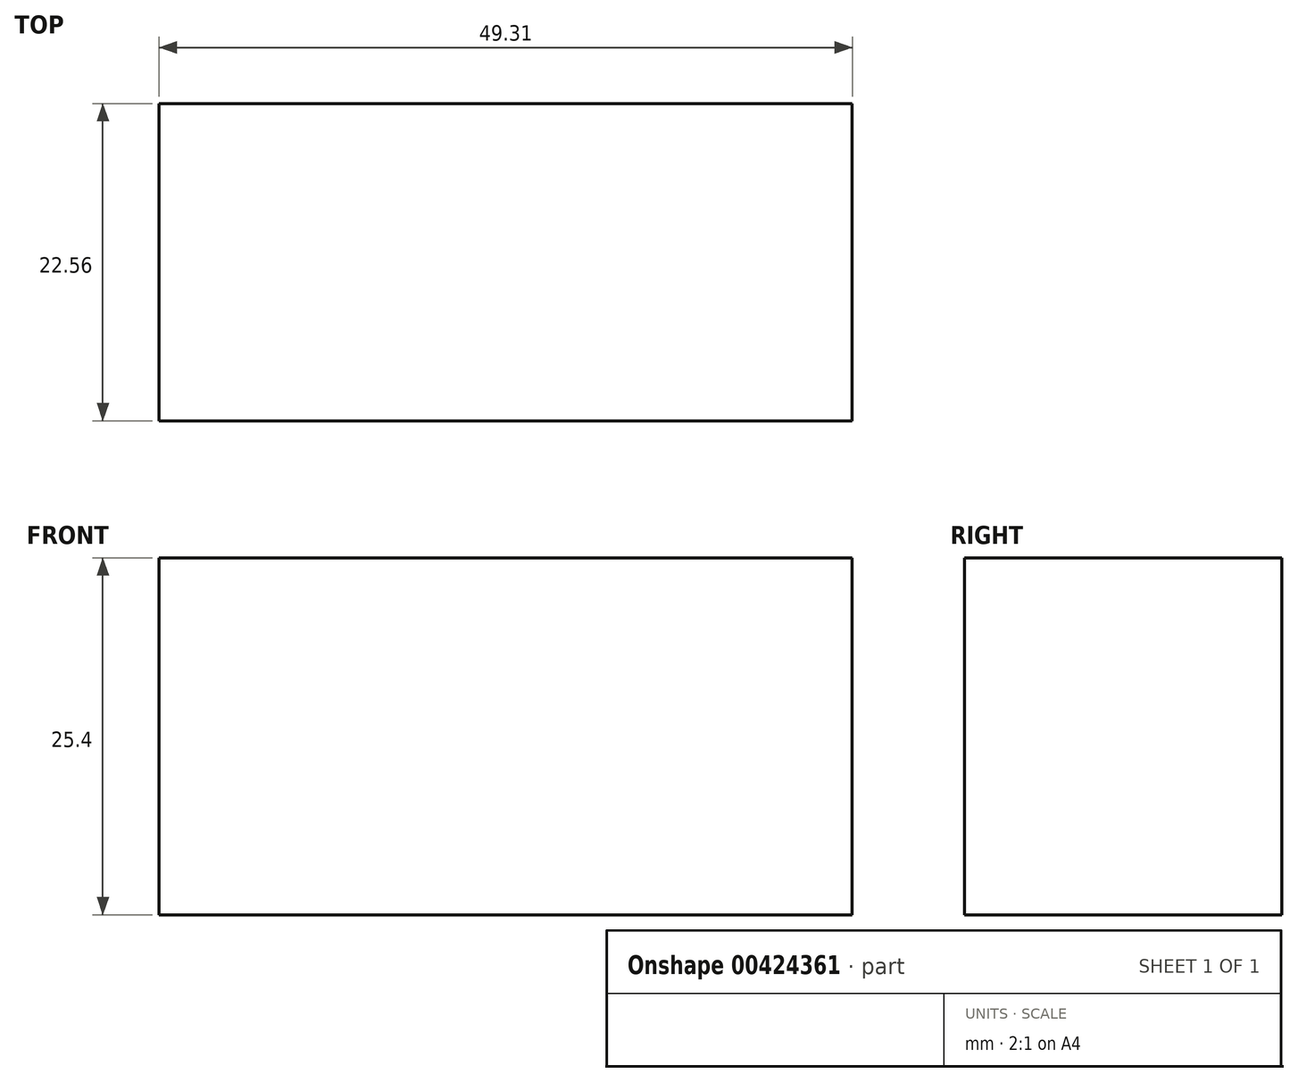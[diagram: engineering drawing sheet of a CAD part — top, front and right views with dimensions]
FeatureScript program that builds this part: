
annotation { "Feature Type Name" : "Feature", "Feature Type Description" : "" }
export const myFeature = defineFeature(function(context is Context, id is Id, definition is map)
    precondition{}
    {
        {
            var Q0;
            Q0=qCreatedBy(makeId("Top.planeOp"),FACE);
            var sketch = newSketch(context, id + "F0", { "sketchPlane" : qUnion([Q0])});
            skLineSegment(sketch, "E0.bottom", {"start": v(0, 0) * mm, "end": v(49.3, 0) * mm});
            skLineSegment(sketch, "E0.top", {"start": v(0, -22.56) * mm, "end": v(49.3, -22.56) * mm});
            skLineSegment(sketch, "E0.left", {"start": v(0, 0) * mm, "end": v(0, -22.56) * mm});
            skLineSegment(sketch, "E0.right", {"start": v(49.3, 0) * mm, "end": v(49.3, -22.56) * mm});
            skSolve(sketch);
        }
        {
            var Q0;
            Q0=makeQuery(id+"F0.imprint","IMPRINT",FACE,{"disambiguationData":[TD([[makeQuery(id+"F0.imprint","IMPRINT",EDGE,{"derivedFrom":sQuery(id+"F0.wireOp",EDGE,"E0.bottom")}),-1.0]])]});
            extrude(context, id + "F1", {"entities" : qUnion([Q0]), "depth" : 25.4 * mm});
        }
    });
